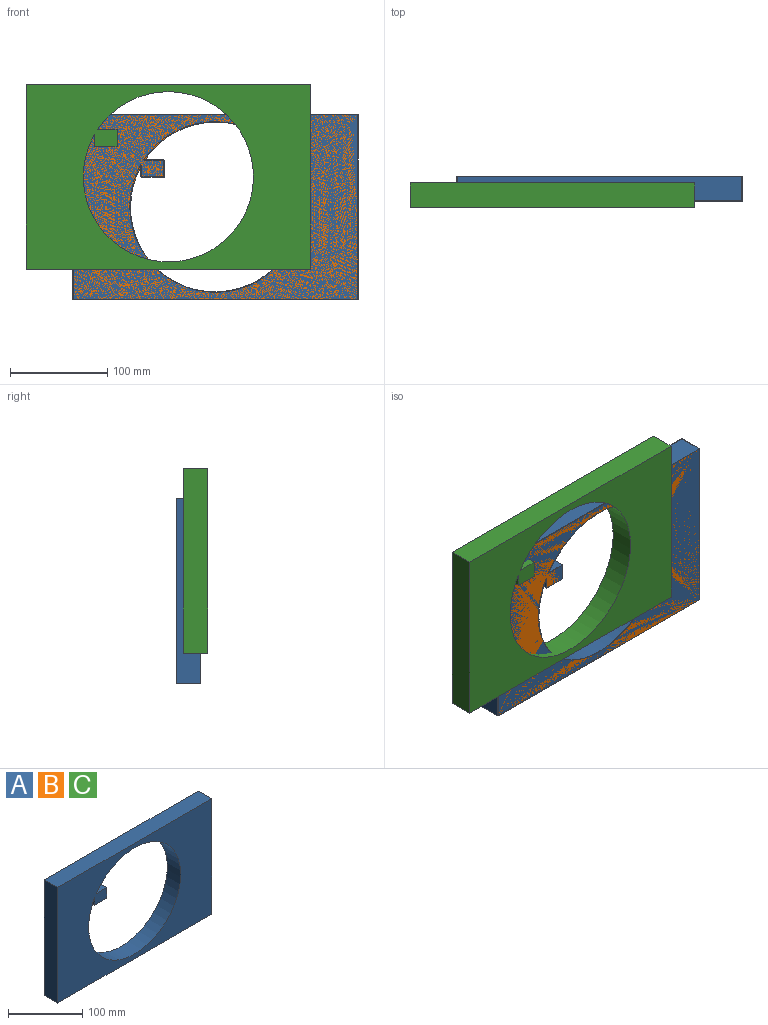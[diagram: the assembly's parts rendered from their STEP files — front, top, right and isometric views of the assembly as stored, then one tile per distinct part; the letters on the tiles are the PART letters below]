
ASSEMBLY  parts=3 mates=1
PART A: 11 faces, bbox 292.8x25.4x190.2 mm
  f0: plane 25.4x23.32mm, normal (0,0,-1), area 592.3mm2, adj f1,f3,f4,f5
  f1: plane 25.4x17.6mm, normal (1,0,0), area 447mm2, adj f0,f2,f4,f5
  f2: plane 25.4x20.21mm, normal (0,0,1), area 513.3mm2, adj f1,f4,f5,f6
  f3: plane 25.4x12.54mm, normal (-1,0,0), area 318.5mm2, adj f0,f4,f5,f6
  f4: plane 292.81x190.18mm, normal (0,-1,0), area 32018.7mm2, adj f0,f1,f2,f3,f6,f7,f8,f9
  f5: plane 292.81x190.18mm, normal (0,1,0), area 32018.7mm2, adj f0,f1,f2,f3,f6,f7,f8,f9
  f6: cylinder r=87.53mm len=175.06mm, axis (0,1,0), area 13818.5mm2, adj f2,f3,f4,f5
  f7: plane 292.81x25.4mm, normal (0,0,1), area 7437.4mm2, adj f4,f5,f8,f10
  f8: plane 190.18x25.4mm, normal (-1,0,0), area 4830.5mm2, adj f4,f5,f7,f9
  f9: plane 292.81x25.4mm, normal (0,0,-1), area 7437.4mm2, adj f4,f5,f8,f10
  f10: plane 190.18x25.4mm, normal (1,0,0), area 4830.5mm2, adj f4,f5,f7,f9
PART B: same geometry as A
PART C: same geometry as A
PLACE A t=(58.11,48.56,19.7)mm fixed
PLACE B t=(58.92,48.56,19.21)mm
PLACE C t=(10.22,41.47,50.54)mm
MATE planar B.f4 <-> A.f6  axis (0,-1,0) through (58.11,23.16,19.7)mm
